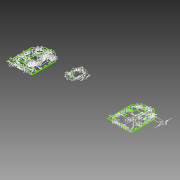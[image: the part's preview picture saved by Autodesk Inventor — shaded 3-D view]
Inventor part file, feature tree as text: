
AUTODESK INVENTOR PART (.ipt)
format: ipt  version: 2012 (Build 160160000, 160)  size: 236,544 bytes
history: native  units: mm
features: sketch x1
ambient origin geometry x8: Origin, YZ Plane, XZ Plane, XY Plane, X Axis, Y Axis, Z Axis, Center Point
feature tree (1):
  sketch  "Sketch1"  dims[d12=10.0mm d13=2.0mm d16=10.0mm d17=2.0mm d19=10.0mm d20=2.0mm d23=10.0mm d24=2.0mm d25=10.0mm d26=10.0mm d27=2.0mm d28=10.0mm d29=2.0mm d30=10.0mm d33=15.0mm d34=2.0mm d36=15.0mm d37=18.0mm d38=15.0mm d39=17.0mm d40=2.0mm d41=15.0mm d43=15.0mm d44=18.0mm d45=15.0mm d46=17.0mm d47=15.0mm d48=18.0mm d52=15.0mm d54=18.0mm d55=219.764931mm d56=174.51mm d57=3.0mm d58=3.0mm d59=3.0mm d60=3.0mm d61=3.0mm d62=-5.117mm d63=10.0mm d64=15.117mm d65=10.0mm d66=5.554212mm d67=5.0mm d68=5.0mm d69=5.554212mm d70=5.554212mm d71=5.0mm d72=5.0mm d75=3.0mm d76=3.0mm d77=3.0mm d78=5.117mm d79=0.0mm d80=15.117007mm d81=3.0mm d82=5.0mm d83=5.0mm d84=5.0mm d85=5.000007mm d86=5.0mm d94=57.0mm d95=67.0mm d96=3.0mm d97=3.0mm d98=3.0mm d99=51.0mm d100=51.0mm d101=51.0mm d102=51.0mm d103=3.0mm d104=2.0mm d105=12.0mm d106=12.0mm d107=11.0mm d108=11.0mm d109=3.0mm d110=3.0mm d111=3.0mm d112=2.0mm d113=12.0mm d114=12.0mm d116=11.0mm d118=3.0mm d121=3.0mm d124=10.0mm d125=2.0mm d126=10.0mm d127=2.0mm d128=10.0mm d129=2.0mm d130=10.0mm d131=2.0mm d132=10.0mm d133=10.0mm d134=2.0mm d135=10.0mm d136=2.0mm d137=10.0mm d138=15.0mm d139=2.0mm d140=15.0mm d141=18.0mm d142=15.0mm d143=17.0mm d144=2.0mm d145=15.0mm d146=15.0mm d147=18.0mm d148=15.0mm d149=17.0mm d150=15.0mm d151=18.0mm d152=15.0mm d153=18.0mm d154=219.764931mm d155=174.51mm d156=3.0mm d157=3.0mm d158=71.8mm d159=25.8mm d160=35.0mm d161=16.0mm d163=25.0mm d164=13.0mm d165=21.0mm d166=40.0mm d167=9.7mm d168=20.0mm d203=3.0mm d204=3.0mm d205=95.933639mm d206=95.933639mm d207=95.933639mm d208=50.0mm d211=60.0mm d212=5.0mm d213=110.0mm d214=20.0mm d216=10.0mm d217=5.0mm d248=27.4mm d249=40.4mm d250=3.0mm d251=3.0mm d252=23.7mm d253=39.8mm d254=30.0mm d255=30.0mm d256=5.0mm]
